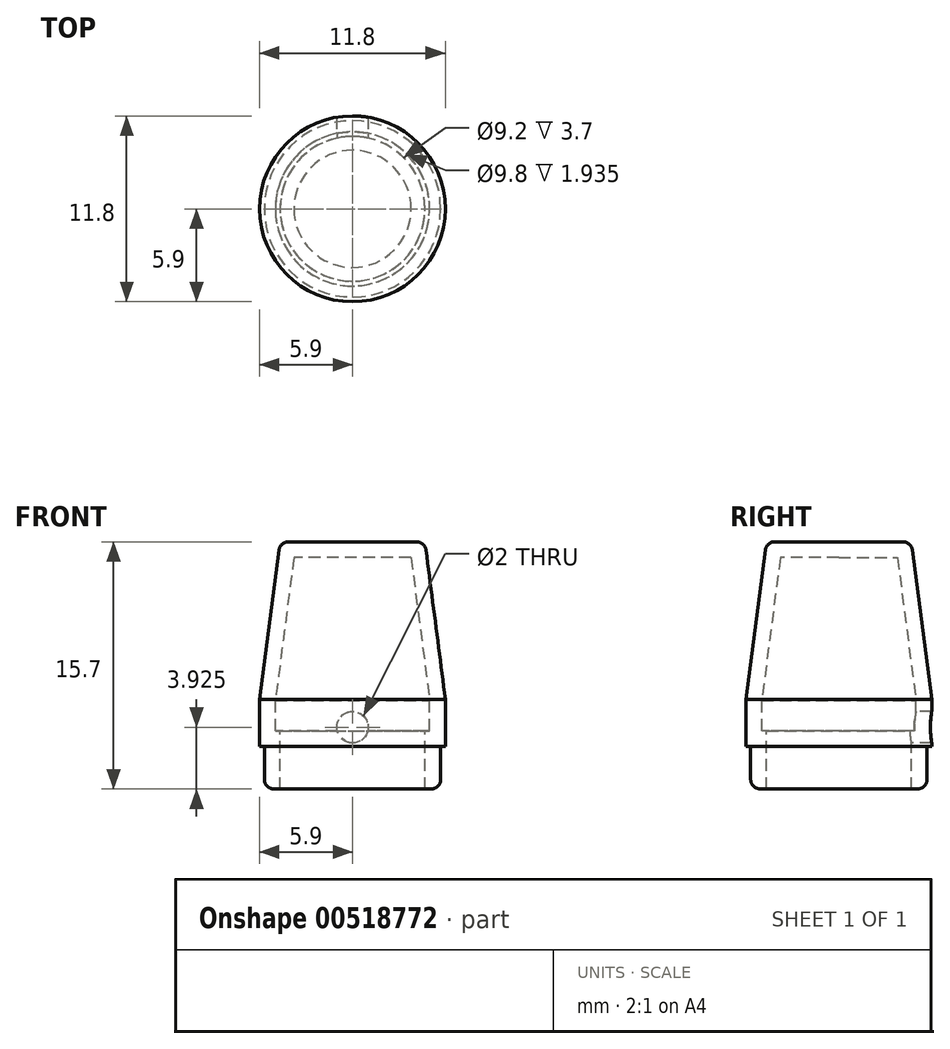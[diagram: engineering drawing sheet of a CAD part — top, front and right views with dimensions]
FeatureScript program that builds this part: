
annotation { "Feature Type Name" : "Feature", "Feature Type Description" : "" }
export const myFeature = defineFeature(function(context is Context, id is Id, definition is map)
    precondition{}
    {
        {
            var Q0;
            Q0=qCreatedBy(makeId("Front.planeOp"),FACE);
            var sketch = newSketch(context, id + "F0", { "sketchPlane" : qUnion([Q0])});
            skLineSegment(sketch, "E0", {"start": v(0, 13) * mm, "end": v(4.6, 13) * mm});
            skLineSegment(sketch, "E1", {"start": v(0, -2.7) * mm, "end": v(5.6, -2.7) * mm});
            skLineSegment(sketch, "E2", {"start": v(5.6, -2.7) * mm, "end": v(5.6, 0) * mm});
            skLineSegment(sketch, "E3", {"start": v(5.6, 0) * mm, "end": v(5.9, 0) * mm});
            skLineSegment(sketch, "E4", {"start": v(0, 13) * mm, "end": v(0, -2.7) * mm});
            skPoint(sketch, "E5", {"position": v(0, 1.23) * mm});
            skLineSegment(sketch, "E6", {"start": v(5.9, 0) * mm, "end": v(5.9, 3) * mm});
            skLineSegment(sketch, "E7", {"start": v(4.6, 13) * mm, "end": v(5.9, 3) * mm});
            skSolve(sketch);
        }
        {
            var Q0;
            Q0=qSketchRegion(id+"F0",true);
            var Q1;
            Q1=sQuery(id+"F0.wireOp",EDGE,"E4");
            revolve(context, id + "F1", {"entities" : qUnion([Q0]), "axis" : qUnion([Q1]), "revolveType" : RevolveType.FULL});
        }
        {
            var Q0;
            Q0=makeQuery(id+"F1.opRevolve","SWEPT_EDGE",EDGE,{"disambiguationData":[OSD([sQuery(id+"F0.wireOp",EDGE,"E0"),sQuery(id+"F0.wireOp",EDGE,"6oBbHD5I-vojS-0J3z-l2ah-PLphUP1hSa3E")])]});
            var Q1;
            Q1=makeQuery(id+"F1.opRevolve","SWEPT_FACE",FACE,{"disambiguationData":[OSD([sQuery(id+"F0.wireOp",EDGE,"E1")])]});
            fillet(context, id + "F2", {"entities" : qUnion([Q0, Q1]), "radius" : 0.6 * mm, "tangentPropagation" : true, "allowEdgeOverflow" : false});
        }
        {
            var Q0;
            Q0=makeQuery(id+"F1.opRevolve","SWEPT_FACE",FACE,{"disambiguationData":[OSD([sQuery(id+"F0.wireOp",EDGE,"E1")])]});
            shell(context, id + "F3", {"entities" : qUnion([Q0]), "thickness" : 1 * mm});
        }
        {
            var Q0;
            Q0=sQuery(id+"F0.wireOp",VERTEX,"E5");
            var Q1;
            Q1=makeQuery(id+"F1.opRevolve","SWEPT_BODY",BODY,{"disambiguationData":[OSD([sQuery(id+"F0.wireOp",EDGE,"E0"),sQuery(id+"F0.wireOp",EDGE,"6oBbHD5I-vojS-0J3z-l2ah-PLphUP1hSa3E"),sQuery(id+"F0.wireOp",EDGE,"E1"),sQuery(id+"F0.wireOp",EDGE,"E2"),sQuery(id+"F0.wireOp",EDGE,"E3"),sQuery(id+"F0.wireOp",EDGE,"E4")])]});
            hole(context, id + "F4", {"style" : HoleStyle.SIMPLE, "endStyle" : HoleEndStyle.THROUGH, "holeDiameter" : 2 * mm, "isTappedThrough" : true, "tappedDepth" : 12 * mm, "tapClearance" : 3, "locations" : qUnion([Q0]), "scope" : qUnion([Q1])});
        }
    });
